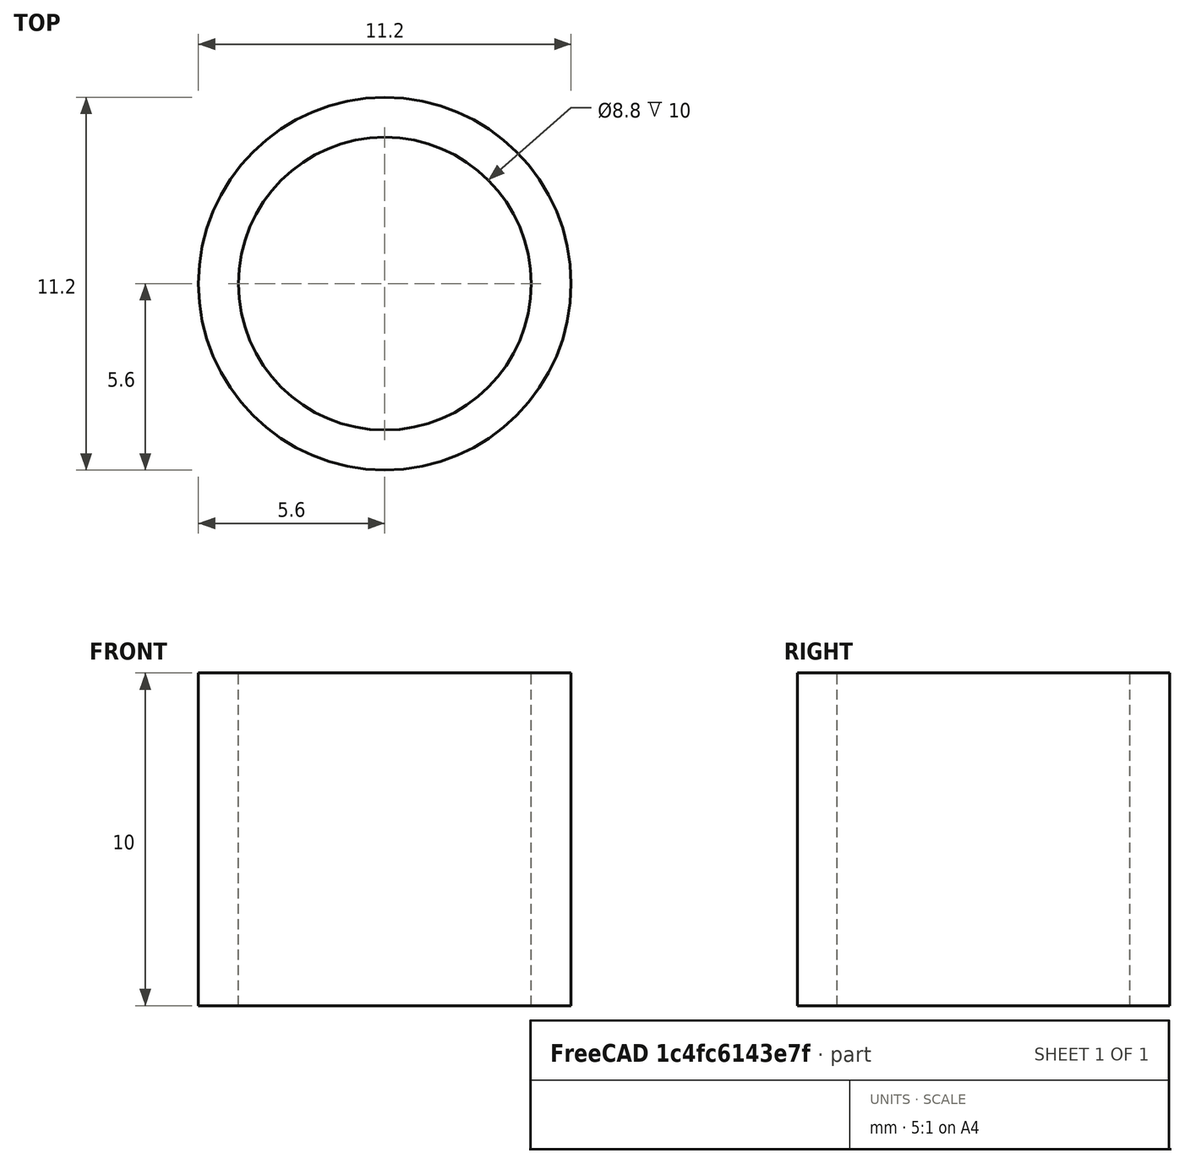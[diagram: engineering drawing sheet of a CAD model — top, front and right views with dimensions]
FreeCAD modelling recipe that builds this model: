
FCSTD DOCUMENT  (FreeCAD 0.20R29177 +426 (Git))
Label: Mag_Spacer
License: All rights reserved
LicenseURL: http://en.wikipedia.org/wiki/All_rights_reserved
objects: Sketcher::SketchObject×1, PartDesign::Revolution×1, PartDesign::Body×1
note: 4 computed .brp shape members not serialized (recipe doc carries the construction recipe); baked Part::Feature solids carry a one-line shape summary decoded from their .brp

FEATURE [Sketcher::SketchObject] Sketch
  FullyConstrained = true
  MapMode = 5
  Placement = pos=(0,0,0) rot=(1,0,0;1.5708rad)
  Support = -> [XZ_Plane]
  sketch-geometry (4):
    g0: LineSegment StartX=-4.4 StartY=0 StartZ=0 EndX=-4.4 EndY=10 EndZ=0
    g1: LineSegment StartX=-5.6 StartY=10 StartZ=0 EndX=-5.6 EndY=0 EndZ=0
    g2: LineSegment StartX=-4.4 StartY=0 StartZ=0 EndX=-5.6 EndY=0 EndZ=0
    g3: LineSegment StartX=-4.4 StartY=10 StartZ=0 EndX=-5.6 EndY=10 EndZ=0
  constraints (12):
    c: Vertical(g0)
    c: Vertical(g1)
    c: Coincident(g2,g0)
    c: Coincident(g2,g1)
    c: Coincident(g3,g0)
    c: Coincident(g3,g1)
    c: Horizontal(g3)
    c: Horizontal(g2)
    c: DistanceX(g2,g2) = 1.2
    c: DistanceY(g0,g0) = 10
    c: Horizontal(g-1,g0)
    c: DistanceX(g0,g-1) = 4.4
FEATURE [PartDesign::Revolution] Revolution
  Angle = 360
  Axis = (0,-2e-16,1)
  Base = (0,0,0)
  Placement = pos=(0,0,0) rot=(1,0,0;1.5708rad)
  Profile = -> Sketch
  ReferenceAxis = -> Sketch [V_Axis]
FEATURE [PartDesign::Body] Body
  Group = -> [Sketch,Revolution]
  Origin = -> Origin
  Tip = -> Revolution
